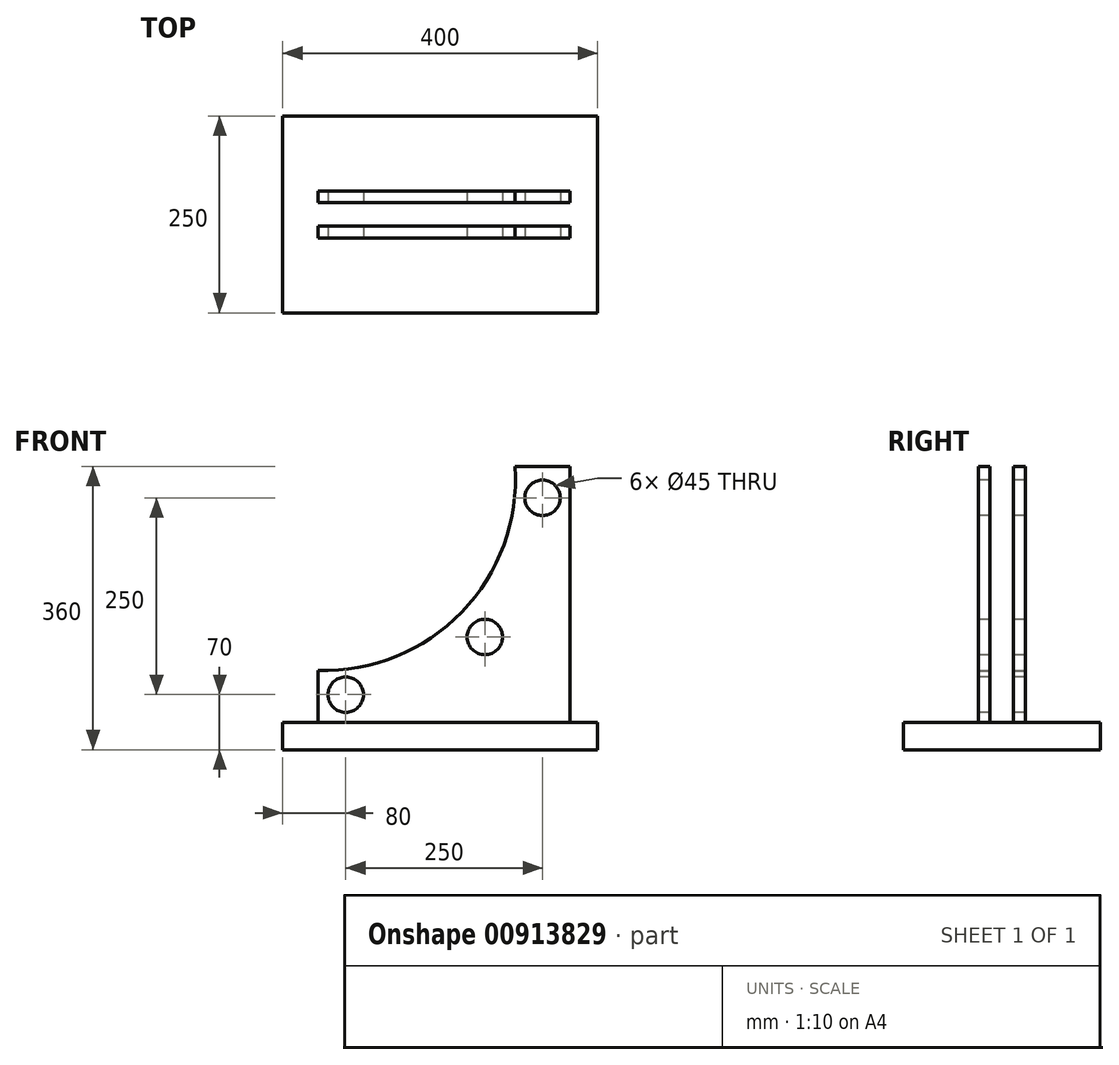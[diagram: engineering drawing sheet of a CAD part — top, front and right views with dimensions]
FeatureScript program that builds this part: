
annotation { "Feature Type Name" : "Feature", "Feature Type Description" : "" }
export const myFeature = defineFeature(function(context is Context, id is Id, definition is map)
    precondition{}
    {
        {
            var Q0;
            Q0=qCreatedBy(makeId("Top.planeOp"),FACE);
            var sketch = newSketch(context, id + "F0", { "sketchPlane" : qUnion([Q0])});
            skLineSegment(sketch, "E0.bottom", {"start": v(-160, -30) * mm, "end": v(160, -30) * mm});
            skLineSegment(sketch, "E0.top", {"start": v(-160, 30) * mm, "end": v(160, 30) * mm});
            skLineSegment(sketch, "E0.left", {"start": v(-160, -30) * mm, "end": v(-160, 30) * mm});
            skLineSegment(sketch, "E0.right", {"start": v(160, -30) * mm, "end": v(160, 30) * mm});
            skLineSegment(sketch, "E1", {"start": v(-160, 30) * mm, "end": v(160, -30) * mm, "construction": true});
            skLineSegment(sketch, "E2", {"start": v(-160, -30) * mm, "end": v(160, 30) * mm, "construction": true});
            skSolve(sketch);
        }
        {
            var Q0;
            Q0=makeQuery(id+"F0.imprint","IMPRINT",FACE,{"disambiguationData":[TD([[makeQuery(id+"F0.imprint","IMPRINT",EDGE,{"derivedFrom":sQuery(id+"F0.wireOp",EDGE,"E0.bottom")}),1.0]])]});
            extrude(context, id + "F1", {"entities" : qUnion([Q0]), "depth" : 360 * mm, "offsetDistance" : 25 * mm});
        }
        {
            var Q0;
            Q0=makeQuery(id+"F1.opExtrude","SWEPT_FACE",FACE,{"disambiguationData":[OSD([sQuery(id+"F0.wireOp",EDGE,"E0.bottom")])]});
            var sketch = newSketch(context, id + "F2", { "sketchPlane" : qUnion([Q0])});
            skCircle(sketch, "E3", {"center": v(125, 320) * mm, "radius": 22.5 * mm});
            skCircle(sketch, "E4", {"center": v(-125, 70) * mm, "radius": 22.5 * mm});
            skCircle(sketch, "E5", {"center": v(51.78, 143.22) * mm, "radius": 22.5 * mm});
            skSolve(sketch);
        }
        {
            var Q0;
            Q0=qSketchRegion(id+"F2",true);
            var Q1;
            Q1=makeQuery(id+"F1.opExtrude","SWEPT_FACE",FACE,{"disambiguationData":[OSD([sQuery(id+"F0.wireOp",EDGE,"E0.top")])]});
            extrude(context, id + "F3", {"entities" : qUnion([Q0]), "operationType" : NewBodyOperationType.REMOVE, "endBound" : BoundingType.UP_TO_SURFACE, "oppositeDirection" : true, "depth" : 25 * mm, "endBoundEntityFace" : qUnion([Q1]), "offsetDistance" : 25 * mm});
        }
        {
            var Q0;
            Q0=qCreatedBy(makeId("Front.planeOp"),FACE);
            var sketch = newSketch(context, id + "F4", { "sketchPlane" : qUnion([Q0])});
            skArc(sketch, "E6", {"start": v(-160, 100.48) * mm, "mid": v(22.48, 174.87) * mm, "end": v(90, 360) * mm});
            skLineSegment(sketch, "E7", {"start": v(0, 0) * mm, "end": v(-160, 360) * mm, "construction": true});
            skLineSegment(sketch, "E8", {"start": v(-160, 100.48) * mm, "end": v(-160, 360) * mm});
            skLineSegment(sketch, "E9", {"start": v(-160, 360) * mm, "end": v(90, 360) * mm});
            skSolve(sketch);
        }
        {
            var Q0;
            Q0=qSketchRegion(id+"F4",true);
            var Q1;
            Q1=makeQuery(id+"F1.opExtrude","SWEPT_FACE",FACE,{"disambiguationData":[OSD([sQuery(id+"F0.wireOp",EDGE,"E0.bottom")])]});
            var Q2;
            Q2=makeQuery(id+"F1.opExtrude","SWEPT_FACE",FACE,{"disambiguationData":[OSD([sQuery(id+"F0.wireOp",EDGE,"E0.top")])]});
            extrude(context, id + "F5", {"entities" : qUnion([Q0]), "operationType" : NewBodyOperationType.REMOVE, "endBound" : BoundingType.UP_TO_SURFACE, "depth" : 25 * mm, "endBoundEntityFace" : qUnion([Q1]), "offsetDistance" : 25 * mm, "hasSecondDirection" : true, "secondDirectionBound" : SecondDirectionBoundingType.UP_TO_SURFACE, "secondDirectionOppositeDirection" : true, "secondDirectionDepth" : 25 * mm, "secondDirectionBoundEntityFace" : qUnion([Q2])});
        }
        {
            var Q0;
            Q0=qCreatedBy(makeId("Right.planeOp"),FACE);
            var sketch = newSketch(context, id + "F6", { "sketchPlane" : qUnion([Q0])});
            skLineSegment(sketch, "E10.bottom", {"start": v(15, 0) * mm, "end": v(-15, 0) * mm});
            skLineSegment(sketch, "E10.top", {"start": v(15, 360) * mm, "end": v(-15, 360) * mm});
            skLineSegment(sketch, "E10.left", {"start": v(-15, 0) * mm, "end": v(-15, 360) * mm});
            skLineSegment(sketch, "E10.right", {"start": v(15, 0) * mm, "end": v(15, 360) * mm});
            skSolve(sketch);
        }
        {
            var Q0;
            Q0=makeQuery(id+"F6.imprint","IMPRINT",FACE,{"disambiguationData":[TD([[makeQuery(id+"F6.imprint","IMPRINT",EDGE,{"derivedFrom":sQuery(id+"F6.wireOp",EDGE,"E10.bottom")}),-1.0]])]});
            var Q1;
            Q1=makeQuery(id+"F1.opExtrude","SWEPT_FACE",FACE,{"disambiguationData":[OSD([sQuery(id+"F0.wireOp",EDGE,"E0.left")])]});
            var Q2;
            Q2=makeQuery(id+"F1.opExtrude","SWEPT_FACE",FACE,{"disambiguationData":[OSD([sQuery(id+"F0.wireOp",EDGE,"E0.right")])]});
            extrude(context, id + "F7", {"entities" : qUnion([Q0]), "operationType" : NewBodyOperationType.REMOVE, "endBound" : BoundingType.UP_TO_SURFACE, "oppositeDirection" : true, "depth" : 25 * mm, "endBoundEntityFace" : qUnion([Q1]), "offsetDistance" : 25 * mm, "hasSecondDirection" : true, "secondDirectionBound" : SecondDirectionBoundingType.UP_TO_SURFACE, "secondDirectionOppositeDirection" : false, "secondDirectionDepth" : 25 * mm, "secondDirectionBoundEntityFace" : qUnion([Q2])});
        }
        {
            var Q0;
            {var subQ0=sQuery(id+"F0.wireOp",EDGE,"E0.bottom");var subQ1=sQuery(id+"F0.wireOp",EDGE,"E0.right");var subQ2=sQuery(id+"F0.wireOp",EDGE,"E0.left");Q0=makeQuery(id+"F7.boolean.opBoolean","SPLIT",FACE,{"disambiguationData":[TD([makeQuery(id+"F1.opExtrude","SWEPT_FACE",FACE,{"disambiguationData":[OSD([subQ0])]})])],"derivedFrom":makeQuery(id+"F1.opExtrude","CAP_FACE",FACE,{"disambiguationData":[OSD([subQ0,sQuery(id+"F0.wireOp",EDGE,"E0.top"),subQ2,subQ1])],"isStart":true})});}
            var sketch = newSketch(context, id + "F8", { "sketchPlane" : qUnion([Q0])});
            skLineSegment(sketch, "E11.bottom", {"start": v(-205, 125) * mm, "end": v(195, 125) * mm});
            skLineSegment(sketch, "E11.top", {"start": v(-205, -125) * mm, "end": v(195, -125) * mm});
            skLineSegment(sketch, "E11.left", {"start": v(-205, 125) * mm, "end": v(-205, -125) * mm});
            skLineSegment(sketch, "E11.right", {"start": v(195, 125) * mm, "end": v(195, -125) * mm});
            skSolve(sketch);
        }
        {
            var Q0;
            Q0=makeQuery(id+"F8.imprint","IMPRINT",FACE,{"disambiguationData":[TD([[makeQuery(id+"F8.imprint","IMPRINT",EDGE,{"derivedFrom":sQuery(id+"F8.wireOp",EDGE,"E11.bottom")}),-1.0]])]});
            extrude(context, id + "F9", {"entities" : qUnion([Q0]), "operationType" : NewBodyOperationType.ADD, "oppositeDirection" : true, "depth" : 35 * mm, "offsetDistance" : 25 * mm});
        }
    });
